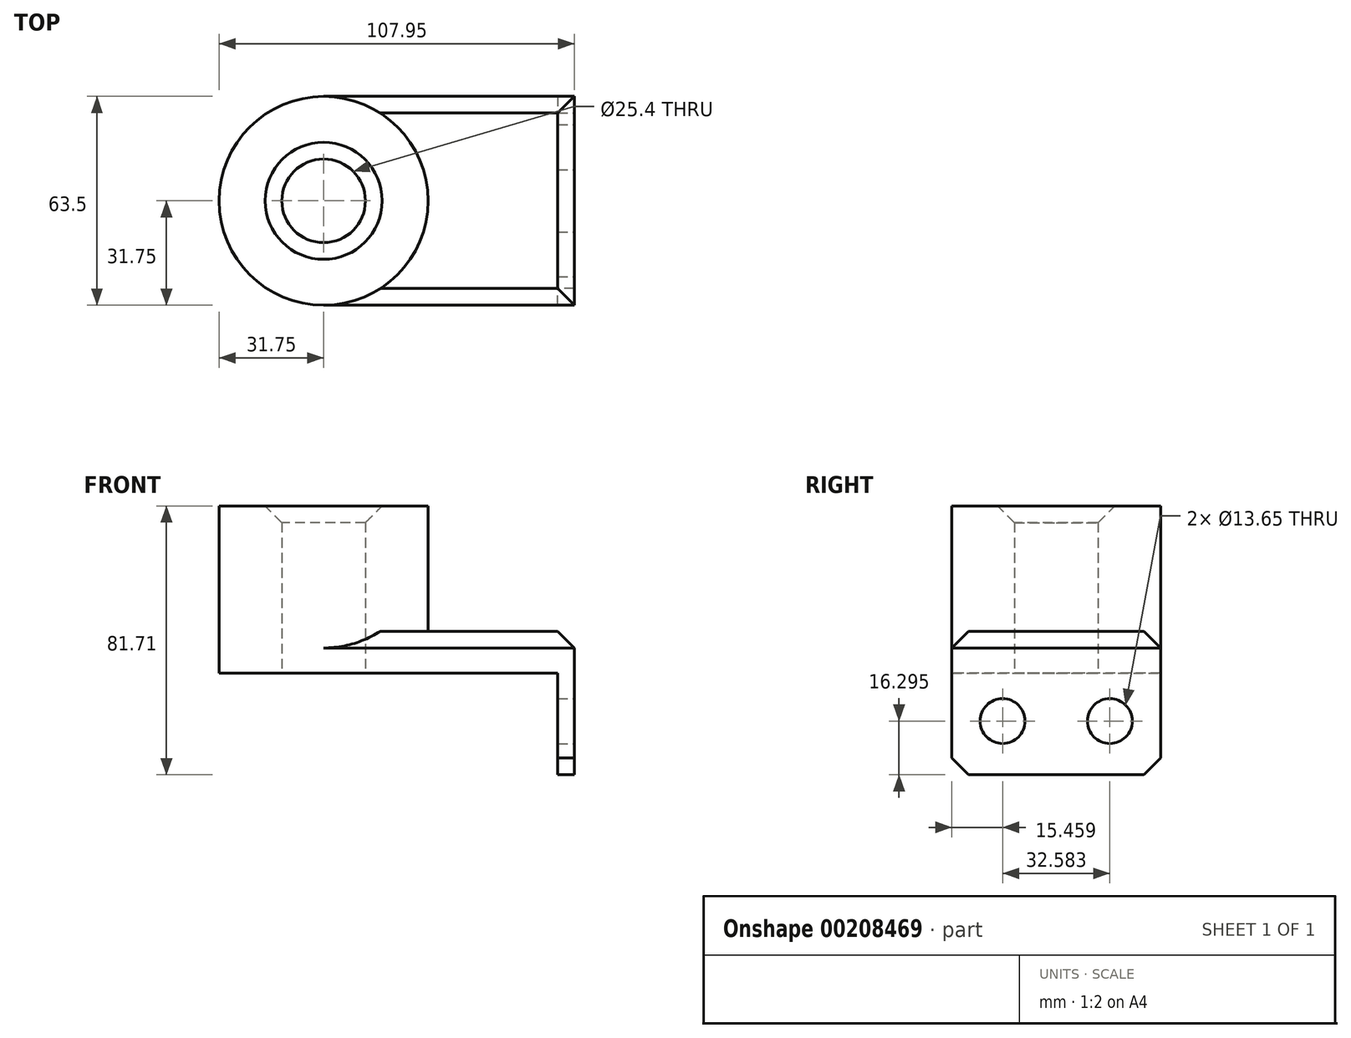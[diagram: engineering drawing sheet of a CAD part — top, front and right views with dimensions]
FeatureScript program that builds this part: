
annotation { "Feature Type Name" : "Feature", "Feature Type Description" : "" }
export const myFeature = defineFeature(function(context is Context, id is Id, definition is map)
    precondition{}
    {
        {
            var Q0;
            Q0=qCreatedBy(makeId("Top.planeOp"),FACE);
            var sketch = newSketch(context, id + "F0", { "sketchPlane" : qUnion([Q0])});
            skLineSegment(sketch, "E0.bottom", {"start": v(38.1, -31.75) * mm, "end": v(-38.1, -31.75) * mm});
            skLineSegment(sketch, "E0.top", {"start": v(38.1, 31.75) * mm, "end": v(-38.1, 31.75) * mm});
            skLineSegment(sketch, "E0.left", {"start": v(38.1, -31.75) * mm, "end": v(38.1, 31.75) * mm});
            skLineSegment(sketch, "E0.right", {"start": v(-38.1, -31.75) * mm, "end": v(-38.1, 31.75) * mm});
            skPoint(sketch, "E0.middle", {"position": v(0, 0) * mm});
            skCircle(sketch, "E1", {"center": v(-38.1, 0) * mm, "radius": 31.75 * mm});
            skCircle(sketch, "E2", {"center": v(-38.1, 0) * mm, "radius": 12.7 * mm});
            skSolve(sketch);
        }
        {
            var Q0;
            Q0 = qSketchRegion(id + "F0", true);
            extrude(context, id + "F1", {"entities" : qUnion([Q0]), "depth" : 12.7 * mm});
        }
        {
            var Q0;
            {var subQ1=sQuery(id+"F0.wireOp",EDGE,"E0.right");var subQ3=sQuery(id+"F0.wireOp",EDGE,"E2");var subQ4=makeQuery(id+"F0.imprint","INTERSECT",VERTEX,{"disambiguationData":[OD(0.0)],"derivedFrom":[subQ1,subQ3]});Q0=makeQuery(id+"F0.imprint","IMPRINT",FACE,{"disambiguationData":[TD([[makeQuery(id+"F0.imprint","IMPRINT",EDGE,{"disambiguationData":[TD([[subQ4,-1.0]])],"derivedFrom":subQ3}),-1.0]])]});}
            var Q1;
            {var subQ1=sQuery(id+"F0.wireOp",EDGE,"E0.right");var subQ3=sQuery(id+"F0.wireOp",EDGE,"E2");var subQ4=makeQuery(id+"F0.imprint","INTERSECT",VERTEX,{"disambiguationData":[OD(0.0)],"derivedFrom":[subQ1,subQ3]});Q1=makeQuery(id+"F0.imprint","IMPRINT",FACE,{"disambiguationData":[TD([[makeQuery(id+"F0.imprint","IMPRINT",EDGE,{"disambiguationData":[TD([[subQ4,1.0]])],"derivedFrom":subQ3}),-1.0]])]});}
            extrude(context, id + "F2", {"entities" : qUnion([Q0, Q1]), "operationType" : NewBodyOperationType.ADD, "depth" : 50.8 * mm});
        }
        {
            var Q0;
            Q0=makeQuery(id+"F1.opExtrude","SWEPT_FACE",FACE,{"disambiguationData":[OSD([sQuery(id+"F0.wireOp",EDGE,"E0.left")])]});
            var sketch = newSketch(context, id + "F3", { "sketchPlane" : qUnion([Q0])});
            skLineSegment(sketch, "E3.bottom", {"start": v(-31.75, 12.7) * mm, "end": v(31.75, 12.7) * mm});
            skLineSegment(sketch, "E3.top", {"start": v(-31.75, -30.9) * mm, "end": v(31.75, -30.9) * mm});
            skLineSegment(sketch, "E3.left", {"start": v(-31.75, 12.7) * mm, "end": v(-31.75, -30.9) * mm});
            skLineSegment(sketch, "E3.right", {"start": v(31.75, 12.7) * mm, "end": v(31.75, -30.9) * mm});
            skCircle(sketch, "E4", {"center": v(-16.3, -14.62) * mm, "radius": 6.82 * mm});
            skLineSegment(sketch, "E5", {"start": v(0, 0) * mm, "end": v(0, -30.9) * mm, "construction": true});
            skCircle(sketch, "E6.MirrorC", {"center": v(16.3, -14.62) * mm, "radius": 6.82 * mm});
            skSolve(sketch);
        }
        {
            var Q0;
            {var subQ2=sQuery(id+"F3.wireOp",EDGE,"E3.top");Q0=makeQuery(id+"F3.imprint","IMPRINT",FACE,{"disambiguationData":[TD([[makeQuery(id+"F3.imprint","IMPRINT",EDGE,{"derivedFrom":subQ2}),1.0]])]});}
            extrude(context, id + "F4", {"entities" : qUnion([Q0]), "operationType" : NewBodyOperationType.ADD, "oppositeDirection" : true, "depth" : 5.08 * mm});
        }
        {
            var Q0;
            Q0=makeQuery(id+"F1.opExtrude","CAP_EDGE",EDGE,{"disambiguationData":[OSD([sQuery(id+"F0.wireOp",EDGE,"E0.left")])],"isStart":false});
            var Q1;
            Q1=makeQuery(id+"F4.opExtrude","SWEPT_EDGE",EDGE,{"disambiguationData":[OSD([sQuery(id+"F3.wireOp",EDGE,"E3.top"),sQuery(id+"F3.wireOp",EDGE,"E3.left")])]});
            var Q2;
            Q2=makeQuery(id+"F4.opExtrude","SWEPT_EDGE",EDGE,{"disambiguationData":[OSD([sQuery(id+"F3.wireOp",EDGE,"E3.top"),sQuery(id+"F3.wireOp",EDGE,"E3.right")])]});
            var Q3;
            Q3=makeQuery(id+"F2.opExtrude","CAP_EDGE",EDGE,{"disambiguationData":[OSD([sQuery(id+"F0.wireOp",EDGE,"E2")])],"isStart":false});
            var Q4;
            Q4=makeQuery(id+"F1.opExtrude","CAP_EDGE",EDGE,{"disambiguationData":[OSD([sQuery(id+"F0.wireOp",EDGE,"E0.bottom")])],"isStart":false});
            var Q5;
            Q5=makeQuery(id+"F1.opExtrude","CAP_EDGE",EDGE,{"disambiguationData":[OSD([sQuery(id+"F0.wireOp",EDGE,"E0.top")])],"isStart":false});
            chamfer(context, id + "F5", {"entities" : qUnion([Q0, Q1, Q2, Q3, Q4, Q5]), "width" : 5.08 * mm, "tangentPropagation" : true});
        }
    });
